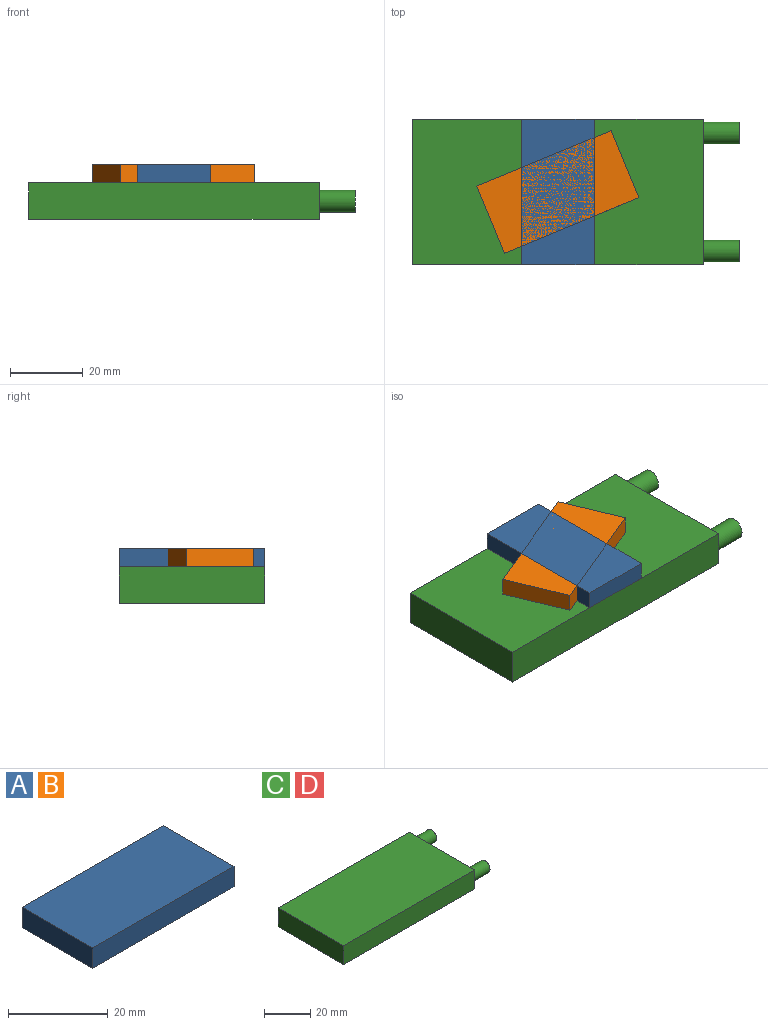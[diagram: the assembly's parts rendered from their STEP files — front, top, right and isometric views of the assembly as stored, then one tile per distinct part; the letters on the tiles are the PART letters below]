
ASSEMBLY  parts=4 mates=2
PART A: 6 faces, bbox 40x20x5 mm
  f0: plane 20x5mm, normal (1,0,0), area 100mm2, adj f1,f3,f4,f5
  f1: plane 40x5mm, normal (0,1,0), area 200mm2, adj f0,f2,f4,f5
  f2: plane 20x5mm, normal (-1,0,0), area 100mm2, adj f1,f3,f4,f5
  f3: plane 40x5mm, normal (0,-1,0), area 200mm2, adj f0,f2,f4,f5
  f4: plane 40x20mm, normal (0,0,1), area 800mm2, adj f0,f1,f2,f3
  f5: plane 40x20mm, normal (0,0,-1), area 800mm2, adj f0,f1,f2,f3
PART B: same geometry as A
PART C: 10 faces, bbox 90x40x10 mm
  f0: plane 80x10mm, normal (0,1,0), area 800mm2, adj f1,f3,f4,f5
  f1: plane 40x10mm, normal (-1,0,0), area 400mm2, adj f0,f2,f4,f5
  f2: plane 80x10mm, normal (0,-1,0), area 800mm2, adj f1,f3,f4,f5
  f3: plane 40x10mm, normal (1,0,0), area 343.2mm2, adj f0,f2,f4,f5,f6,f8
  f4: plane 80x40mm, normal (0,0,1), area 3200mm2, adj f0,f1,f2,f3
  f5: plane 80x40mm, normal (0,0,-1), area 3200mm2, adj f0,f1,f2,f3
  f6: cylinder r=3.01mm len=10mm, axis (-1,0,0), area 189mm2, adj f3,f7
  f7: plane 6.02x6.02mm, normal (1,0,0), area 28.4mm2, adj f6
  f8: cylinder r=3.01mm len=10mm, axis (-1,0,0), area 189mm2, adj f3,f9
  f9: plane 6.02x6.02mm, normal (1,0,0), area 28.4mm2, adj f8
PART D: same geometry as C
PLACE A rot(axis=(0.71,-0.71,0),180deg) t=(15.66,-18.65,11.02)mm
PLACE B rot(axis=(0.2,-0.98,0),180deg) t=(59.12,-31.5,11.02)mm
PLACE C t=(8.81,-55.5,-13.98)mm
PLACE D t=(8.81,-55.5,-13.98)mm
MATE revolute A.f4 <-> B.f4  axis (0,0,-1) through (27.77,-57.61,-3.98)mm
MATE fastened A.f4 <-> C.f4  axis (0,0,-1) through (27.77,-57.61,-3.98)mm
